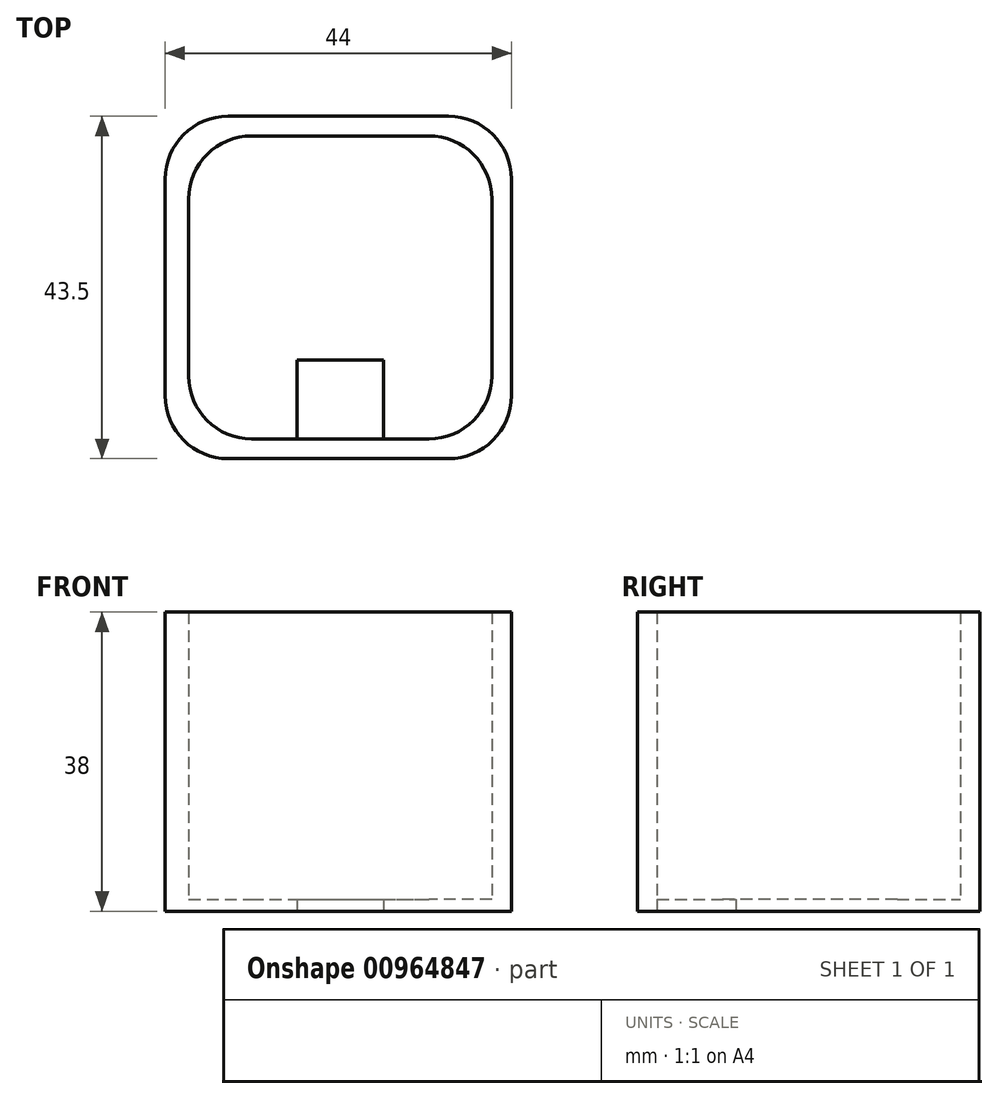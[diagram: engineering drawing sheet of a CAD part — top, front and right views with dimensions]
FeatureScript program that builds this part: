
annotation { "Feature Type Name" : "Feature", "Feature Type Description" : "" }
export const myFeature = defineFeature(function(context is Context, id is Id, definition is map)
    precondition{}
    {
        {
            var Q0;
            Q0=qCreatedBy(makeId("Top.planeOp"),FACE);
            var sketch = newSketch(context, id + "F0", { "sketchPlane" : qUnion([Q0])});
            skLineSegment(sketch, "E0.bottom", {"start": v(-12.35, 16.61) * mm, "end": v(10.15, 16.61) * mm});
            skLineSegment(sketch, "E0.top", {"start": v(-12.35, -21.89) * mm, "end": v(10.15, -21.89) * mm});
            skLineSegment(sketch, "E0.left", {"start": v(-20.35, 8.61) * mm, "end": v(-20.35, -13.89) * mm});
            skLineSegment(sketch, "E0.right", {"start": v(18.15, 8.61) * mm, "end": v(18.15, -13.89) * mm});
            skLineSegment(sketch, "E1.bottom", {"start": v(-15.35, 19.11) * mm, "end": v(12.65, 19.11) * mm});
            skLineSegment(sketch, "E1.top", {"start": v(-15.35, -24.39) * mm, "end": v(12.65, -24.39) * mm});
            skLineSegment(sketch, "E1.left", {"start": v(-23.35, 11.11) * mm, "end": v(-23.35, -16.39) * mm});
            skLineSegment(sketch, "E1.right", {"start": v(20.65, 11.11) * mm, "end": v(20.65, -16.39) * mm});
            skLineSegment(sketch, "E2", {"start": v(-6.6, -21.89) * mm, "end": v(-6.6, -11.89) * mm});
            skLineSegment(sketch, "E3", {"start": v(-6.6, -11.89) * mm, "end": v(4.4, -11.89) * mm});
            skLineSegment(sketch, "E4", {"start": v(4.4, -11.89) * mm, "end": v(4.4, -21.89) * mm});
            skPoint(sketch, "E5.visualSharp", {"position": v(-20.35, 16.61) * mm});
            skArc(sketch, "E5.filletArc", {"start": v(-12.35, 16.61) * mm, "mid": v(-18, 14.27) * mm, "end": v(-20.35, 8.61) * mm});
            skPoint(sketch, "E6.visualSharp", {"position": v(18.15, 16.61) * mm});
            skArc(sketch, "E6.filletArc", {"start": v(18.15, 8.61) * mm, "mid": v(15.8, 14.27) * mm, "end": v(10.15, 16.61) * mm});
            skPoint(sketch, "E7.visualSharp", {"position": v(18.15, -21.89) * mm});
            skArc(sketch, "E7.filletArc", {"start": v(10.15, -21.89) * mm, "mid": v(15.8, -19.55) * mm, "end": v(18.15, -13.89) * mm});
            skPoint(sketch, "E8.visualSharp", {"position": v(-20.35, -21.89) * mm});
            skArc(sketch, "E8.filletArc", {"start": v(-20.35, -13.89) * mm, "mid": v(-18, -19.55) * mm, "end": v(-12.35, -21.89) * mm});
            skPoint(sketch, "E9.visualSharp", {"position": v(-23.35, -24.39) * mm});
            skArc(sketch, "E9.filletArc", {"start": v(-23.35, -16.39) * mm, "mid": v(-21, -22.05) * mm, "end": v(-15.35, -24.39) * mm});
            skPoint(sketch, "E10.visualSharp", {"position": v(20.65, -24.39) * mm});
            skArc(sketch, "E10.filletArc", {"start": v(12.65, -24.39) * mm, "mid": v(18.3, -22.05) * mm, "end": v(20.65, -16.39) * mm});
            skPoint(sketch, "E11.visualSharp", {"position": v(20.65, 19.11) * mm});
            skArc(sketch, "E11.filletArc", {"start": v(20.65, 11.11) * mm, "mid": v(18.3, 16.77) * mm, "end": v(12.65, 19.11) * mm});
            skPoint(sketch, "E12.visualSharp", {"position": v(-23.35, 19.11) * mm});
            skArc(sketch, "E12.filletArc", {"start": v(-15.35, 19.11) * mm, "mid": v(-21, 16.77) * mm, "end": v(-23.35, 11.11) * mm});
            skSolve(sketch);
        }
        {
            var Q0;
            Q0=makeQuery(id+"F0.imprint","IMPRINT",FACE,{"disambiguationData":[TD([[makeQuery(id+"F0.imprint","IMPRINT",EDGE,{"derivedFrom":sQuery(id+"F0.wireOp",EDGE,"E0.bottom")}),1.0]])]});
            extrude(context, id + "F1", {"entities" : qUnion([Q0]), "depth" : 38 * mm, "offsetDistance" : 25 * mm});
        }
        {
            var Q0;
            Q0=makeQuery(id+"F0.imprint","IMPRINT",FACE,{"disambiguationData":[TD([[makeQuery(id+"F0.imprint","IMPRINT",EDGE,{"derivedFrom":sQuery(id+"F0.wireOp",EDGE,"E0.bottom")}),-1.0]])]});
            extrude(context, id + "F2", {"entities" : qUnion([Q0]), "operationType" : NewBodyOperationType.ADD, "depth" : 1.5 * mm, "offsetDistance" : 25 * mm});
        }
    });
